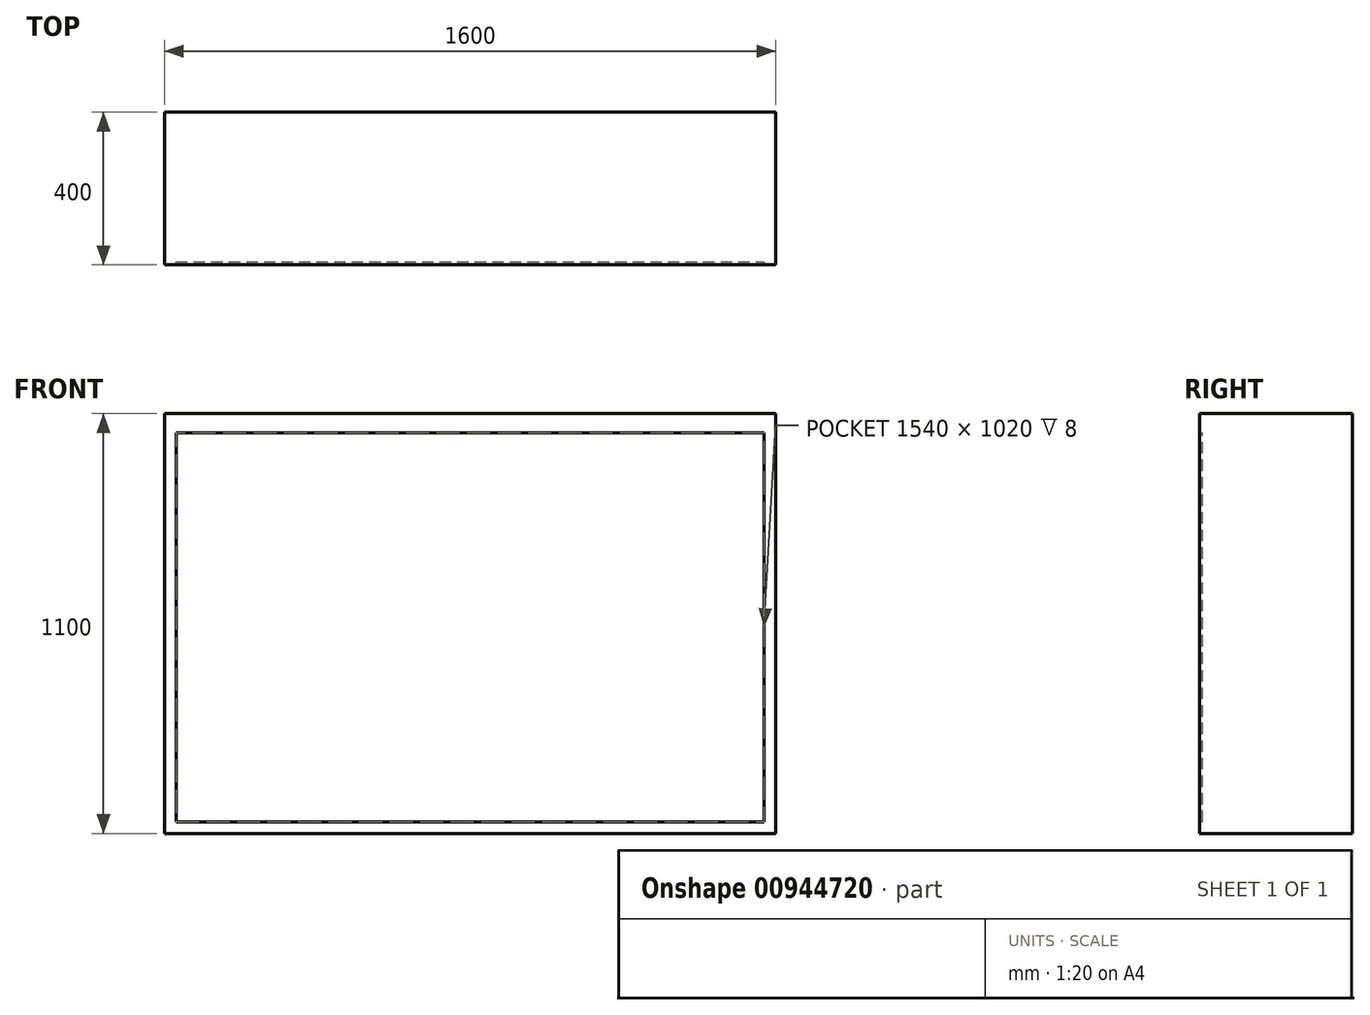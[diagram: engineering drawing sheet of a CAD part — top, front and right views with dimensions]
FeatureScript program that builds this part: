
annotation { "Feature Type Name" : "Feature", "Feature Type Description" : "" }
export const myFeature = defineFeature(function(context is Context, id is Id, definition is map)
    precondition{}
    {
        {
            var Q0;
            Q0=qCreatedBy(makeId("Top.planeOp"),FACE);
            var sketch = newSketch(context, id + "F0", { "sketchPlane" : qUnion([Q0])});
            skLineSegment(sketch, "E0.bottom", {"start": v(0, 0) * mm, "end": v(1600, 0) * mm});
            skLineSegment(sketch, "E0.top", {"start": v(0, -400) * mm, "end": v(1600, -400) * mm});
            skLineSegment(sketch, "E0.left", {"start": v(0, 0) * mm, "end": v(0, -400) * mm});
            skLineSegment(sketch, "E0.right", {"start": v(1600, 0) * mm, "end": v(1600, -400) * mm});
            skSolve(sketch);
        }
        {
            var Q0;
            Q0=makeQuery(id+"F0.imprint","IMPRINT",FACE,{"disambiguationData":[TD([[makeQuery(id+"F0.imprint","IMPRINT",EDGE,{"derivedFrom":sQuery(id+"F0.wireOp",EDGE,"E0.bottom")}),-1.0]])]});
            extrude(context, id + "F1", {"entities" : qUnion([Q0]), "oppositeDirection" : true, "depth" : 1100 * mm, "offsetDistance" : 25 * mm});
        }
        {
            var Q0;
            Q0=makeQuery(id+"F1.opExtrude","CAP_FACE",FACE,{"disambiguationData":[OSD([sQuery(id+"F0.wireOp",EDGE,"E0.bottom"),sQuery(id+"F0.wireOp",EDGE,"E0.top"),sQuery(id+"F0.wireOp",EDGE,"E0.left"),sQuery(id+"F0.wireOp",EDGE,"E0.right")])],"isStart":true});
            var sketch = newSketch(context, id + "F2", { "sketchPlane" : qUnion([Q0])});
            skLineSegment(sketch, "E1.bottom", {"start": v(30, -400) * mm, "end": v(1570, -400) * mm});
            skLineSegment(sketch, "E1.top", {"start": v(30, -392) * mm, "end": v(1570, -392) * mm});
            skLineSegment(sketch, "E1.left", {"start": v(30, -400) * mm, "end": v(30, -392) * mm});
            skLineSegment(sketch, "E1.right", {"start": v(1570, -400) * mm, "end": v(1570, -392) * mm});
            skSolve(sketch);
        }
        {
            var Q0;
            Q0=makeQuery(id+"F2.imprint","IMPRINT",FACE,{"disambiguationData":[TD([[makeQuery(id+"F2.imprint","IMPRINT",EDGE,{"derivedFrom":sQuery(id+"F2.wireOp",EDGE,"E1.bottom")}),1.0]])]});
            extrude(context, id + "F3", {"entities" : qUnion([Q0]), "operationType" : NewBodyOperationType.REMOVE, "endBound" : BoundingType.UP_TO_NEXT, "oppositeDirection" : true, "depth" : 200 * mm, "hasOffset" : true, "offsetDistance" : 30 * mm, "hasSecondDirection" : true, "secondDirectionOppositeDirection" : true, "secondDirectionDepth" : 50 * mm});
        }
    });
